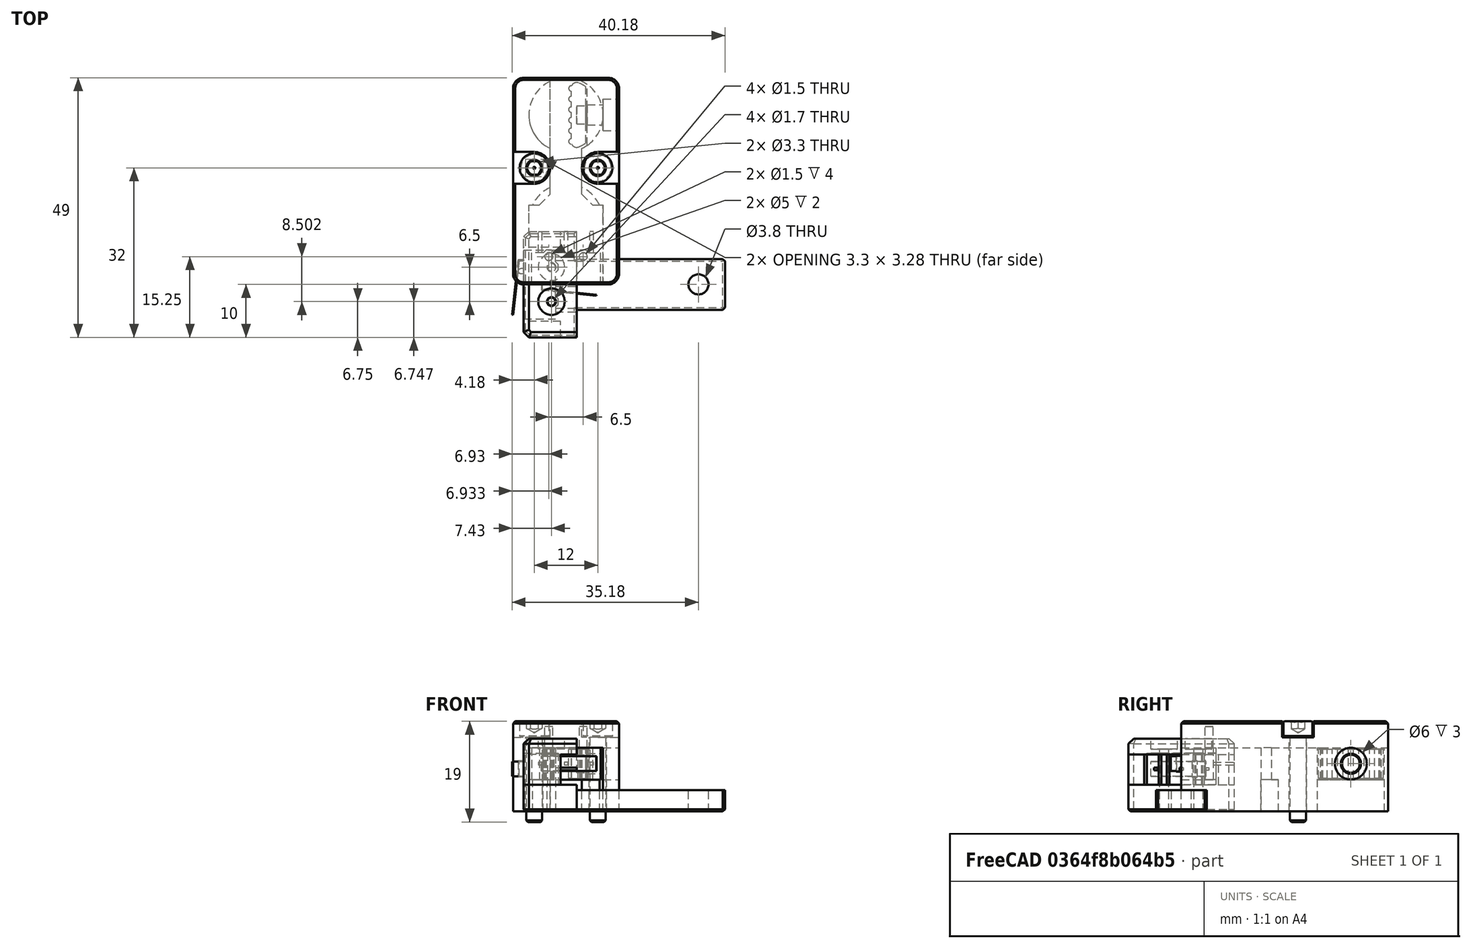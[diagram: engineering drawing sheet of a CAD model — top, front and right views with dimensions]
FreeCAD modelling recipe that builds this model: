
FCSTD DOCUMENT  (FreeCAD 0.19R24291 (Git))
Label: endstop-assembly
License: Other
LicenseURL: GPL3
objects: Part::Feature×6, Part::FeaturePython×2, App::Part×2
note: 8 computed .brp shape members not serialized (recipe doc carries the construction recipe); baked Part::Feature solids carry a one-line shape summary decoded from their .brp

FEATURE [Part::Feature] Cut002008023012009006003002006002006002004004001  label="endstop-mount001"
  shape: bbox 20 x 39 x 17 mm, 57 faces (baked)
FEATURE [Part::Feature] Fusion001001001007  label="switch001"
  Placement = pos=(0,0,6) rot=(0,0,1;0rad)
  shape: bbox 13 x 12.18 x 6 mm, 43 faces (baked)
FEATURE [Part::Feature] Fusion001001001011002001  label="wire-clamp001"
  shape: bbox 3.25 x 12.25 x 5.5 mm, 20 faces (baked)
FEATURE [Part::FeaturePython] Screw  label="M3x16-Screw001"  # Fasteners workbench fastener (typed FeaturePython)
  Placement = pos=(-6,22,14) rot=(0,0,1;0rad)
  baseObject = -> Cut002008023012009006003002006002006002004004001 [Edge108]
  diameter = 4
  invert = false
  length = 6
  lengthCustom = 16
  matchOuter = true
  offset = 0
  thread = false
  type = 33
FEATURE [Part::FeaturePython] Screw001  label="M3x16-Screw"  # Fasteners workbench fastener (typed FeaturePython)
  Placement = pos=(6,22,14) rot=(0,0,1;0rad)
  baseObject = -> Cut002008023012009006003002006002006002004004001 [Edge132]
  diameter = 4
  invert = false
  length = 6
  lengthCustom = 16
  matchOuter = true
  offset = 0
  thread = false
  type = 33
FEATURE [App::Part] Part069  label="Y-endstop"
  Group = -> [Fusion001001001007,Cut002008023012009006003002006002006002004004001,Fusion001001001011002001,Screw001,Screw]
  Origin = -> Origin071
  Placement = pos=(-170,296,335.5) rot=(0,0,1;0rad)
FEATURE [Part::Feature] Fusion006002011004053036004001028003005014029  label="switch003"
  Placement = pos=(-8,2e-15,5) rot=(0,0,-1;1.5708rad)
  shape: bbox 12.18 x 13 x 6 mm, 43 faces (baked)
FEATURE [Part::Feature] Fusion006002011004053036004001028003005014028
  shape: bbox 10 x 20 x 8.75 mm, 25 faces (baked)
FEATURE [Part::Feature] Cut002008023012009006003002006002006002004004005001
  shape: bbox 38 x 20 x 5 mm, 29 faces (baked)
FEATURE [App::Part] Part002  label="X-endstop"
  Group = -> [Fusion006002011004053036004001028003005014028,Fusion006002011004053036004001028003005014029,Cut002008023012009006003002006002006002004004005001]
  Origin = -> Origin002
  Placement = pos=(23.5,203,353) rot=(0,0,1;3.14159rad)
